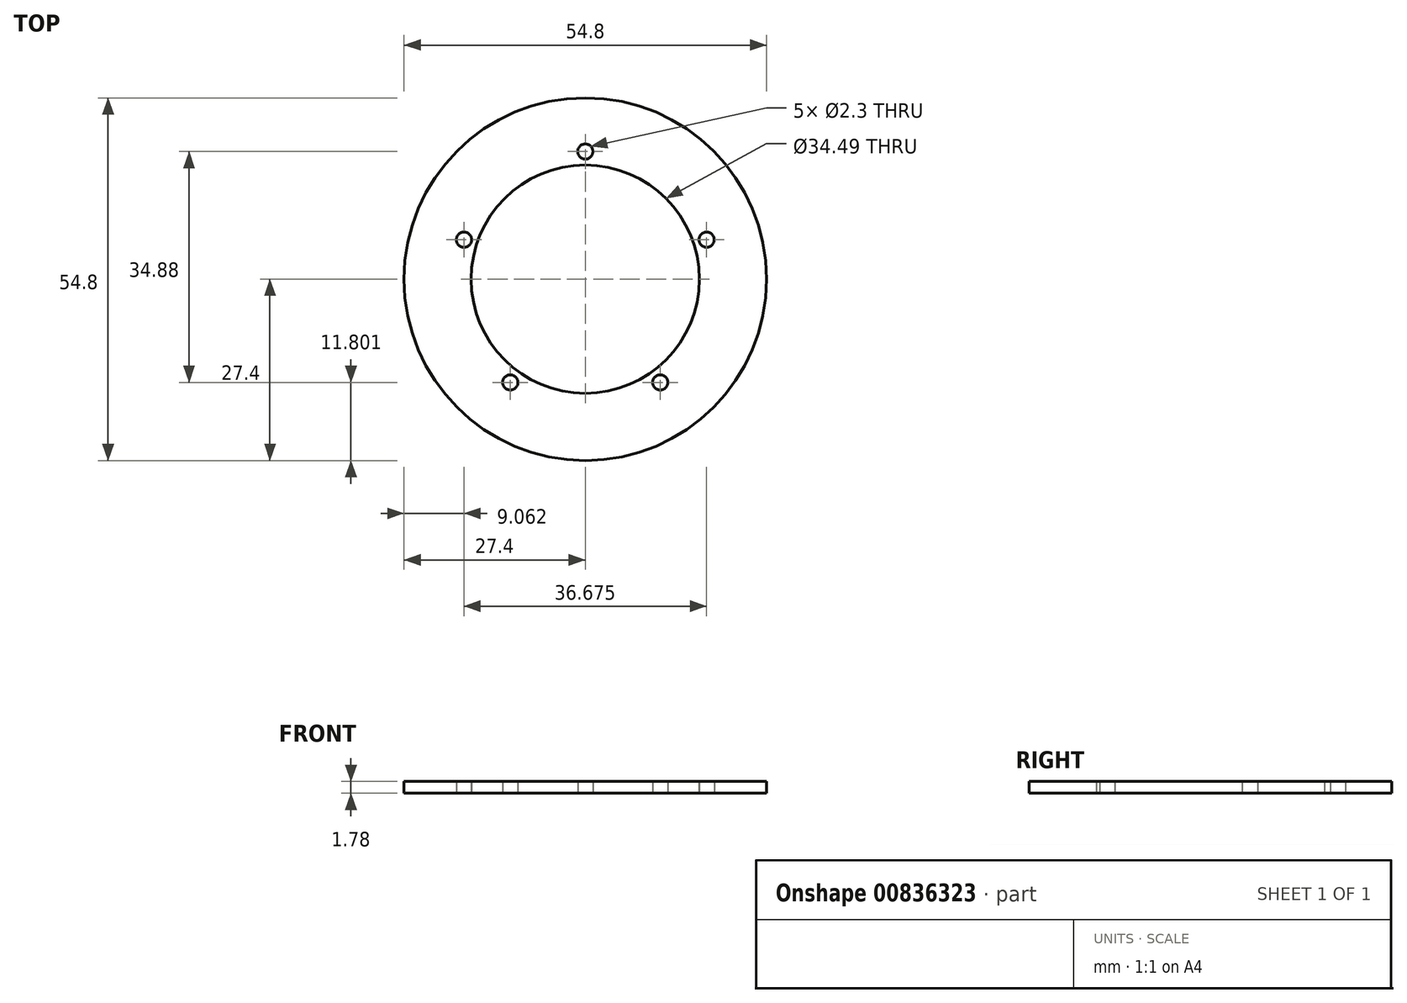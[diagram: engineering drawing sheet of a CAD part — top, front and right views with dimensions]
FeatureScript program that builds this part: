
annotation { "Feature Type Name" : "Feature", "Feature Type Description" : "" }
export const myFeature = defineFeature(function(context is Context, id is Id, definition is map)
    precondition{}
    {
        {
            var Q0;
            Q0=qCreatedBy(makeId("Top.planeOp"),FACE);
            var sketch = newSketch(context, id + "F0", { "sketchPlane" : qUnion([Q0])});
            skCircle(sketch, "E0", {"center": v(0, 0) * mm, "radius": 27.4 * mm});
            skSolve(sketch);
        }
        {
            var Q0;
            Q0=qCreatedBy(makeId("Top.planeOp"),FACE);
            var sketch = newSketch(context, id + "F1", { "sketchPlane" : qUnion([Q0])});
            skCircle(sketch, "E1", {"center": v(0, 0) * mm, "radius": 17.25 * mm});
            skSolve(sketch);
        }
        {
            var Q0;
            Q0 = qSketchRegion(id + "F0", true);
            extrude(context, id + "F2", {"entities" : qUnion([Q0]), "depth" : 1.78 * mm, "offsetDistance" : 25.4 * mm});
        }
        {
            var Q0;
            Q0 = qSketchRegion(id + "F1", true);
            extrude(context, id + "F3", {"entities" : qUnion([Q0]), "operationType" : NewBodyOperationType.REMOVE, "endBound" : BoundingType.UP_TO_NEXT, "depth" : 25.4 * mm, "offsetDistance" : 25.4 * mm});
        }
        {
            var Q0;
            Q0=qCreatedBy(makeId("Front.planeOp"),FACE);
            var sketch = newSketch(context, id + "F4", { "sketchPlane" : qUnion([Q0])});
            skLineSegment(sketch, "E2", {"start": v(0, 77.2) * mm, "end": v(0, -74.83) * mm});
            skSolve(sketch);
        }
        {
            var Q0;
            Q0=qCreatedBy(makeId("Top.planeOp"),FACE);
            var sketch = newSketch(context, id + "F5", { "sketchPlane" : qUnion([Q0])});
            skCircle(sketch, "E3", {"center": v(0, 19.28) * mm, "radius": 1.15 * mm});
            skSolve(sketch);
        }
        {
            var Q0;
            Q0 = qSketchRegion(id + "F5", true);
            extrude(context, id + "F6", {"entities" : qUnion([Q0]), "endBound" : BoundingType.SYMMETRIC, "depth" : 17.78 * mm, "offsetDistance" : 25.4 * mm});
        }
        {
            var Q0;
            Q0=makeQuery(id+"F6.opExtrude","SWEPT_BODY",BODY,{"disambiguationData":[OSD([sQuery(id+"F5.wireOp",EDGE,"E3")])]});
            var Q1;
            Q1=sQuery(id+"F4.wireOp",EDGE,"E2");
            circularPattern(context, id + "F7", {"entities" : qUnion([Q0]), "axis" : qUnion([Q1]), "angle" : 360 * degree, "instanceCount" : 5, "equalSpace" : true});
        }
        {
            var Q0;
            Q0=makeQuery(id+"F7.opPattern","COPY",BODY,{"derivedFrom":makeQuery(id+"F6.opExtrude","SWEPT_BODY",BODY,{"disambiguationData":[OSD([sQuery(id+"F5.wireOp",EDGE,"E3")])]}),"instanceName":"4"});
            var Q1;
            Q1=makeQuery(id+"F6.opExtrude","SWEPT_BODY",BODY,{"disambiguationData":[OSD([sQuery(id+"F5.wireOp",EDGE,"E3")])]});
            var Q2;
            Q2=makeQuery(id+"F7.opPattern","COPY",BODY,{"derivedFrom":makeQuery(id+"F6.opExtrude","SWEPT_BODY",BODY,{"disambiguationData":[OSD([sQuery(id+"F5.wireOp",EDGE,"E3")])]}),"instanceName":"1"});
            var Q3;
            Q3=makeQuery(id+"F7.opPattern","COPY",BODY,{"derivedFrom":makeQuery(id+"F6.opExtrude","SWEPT_BODY",BODY,{"disambiguationData":[OSD([sQuery(id+"F5.wireOp",EDGE,"E3")])]}),"instanceName":"2"});
            var Q4;
            Q4=makeQuery(id+"F7.opPattern","COPY",BODY,{"derivedFrom":makeQuery(id+"F6.opExtrude","SWEPT_BODY",BODY,{"disambiguationData":[OSD([sQuery(id+"F5.wireOp",EDGE,"E3")])]}),"instanceName":"3"});
            var Q5;
            Q5=makeQuery(id+"F2.opExtrude","SWEPT_BODY",BODY,{"disambiguationData":[OSD([sQuery(id+"F0.wireOp",EDGE,"E0")])]});
            booleanBodies(context, id + "F8", {"operationType" : BooleanOperationType.SUBTRACTION, "tools" : qUnion([Q0, Q1, Q2, Q3, Q4]), "targets" : qUnion([Q5])});
        }
    });
